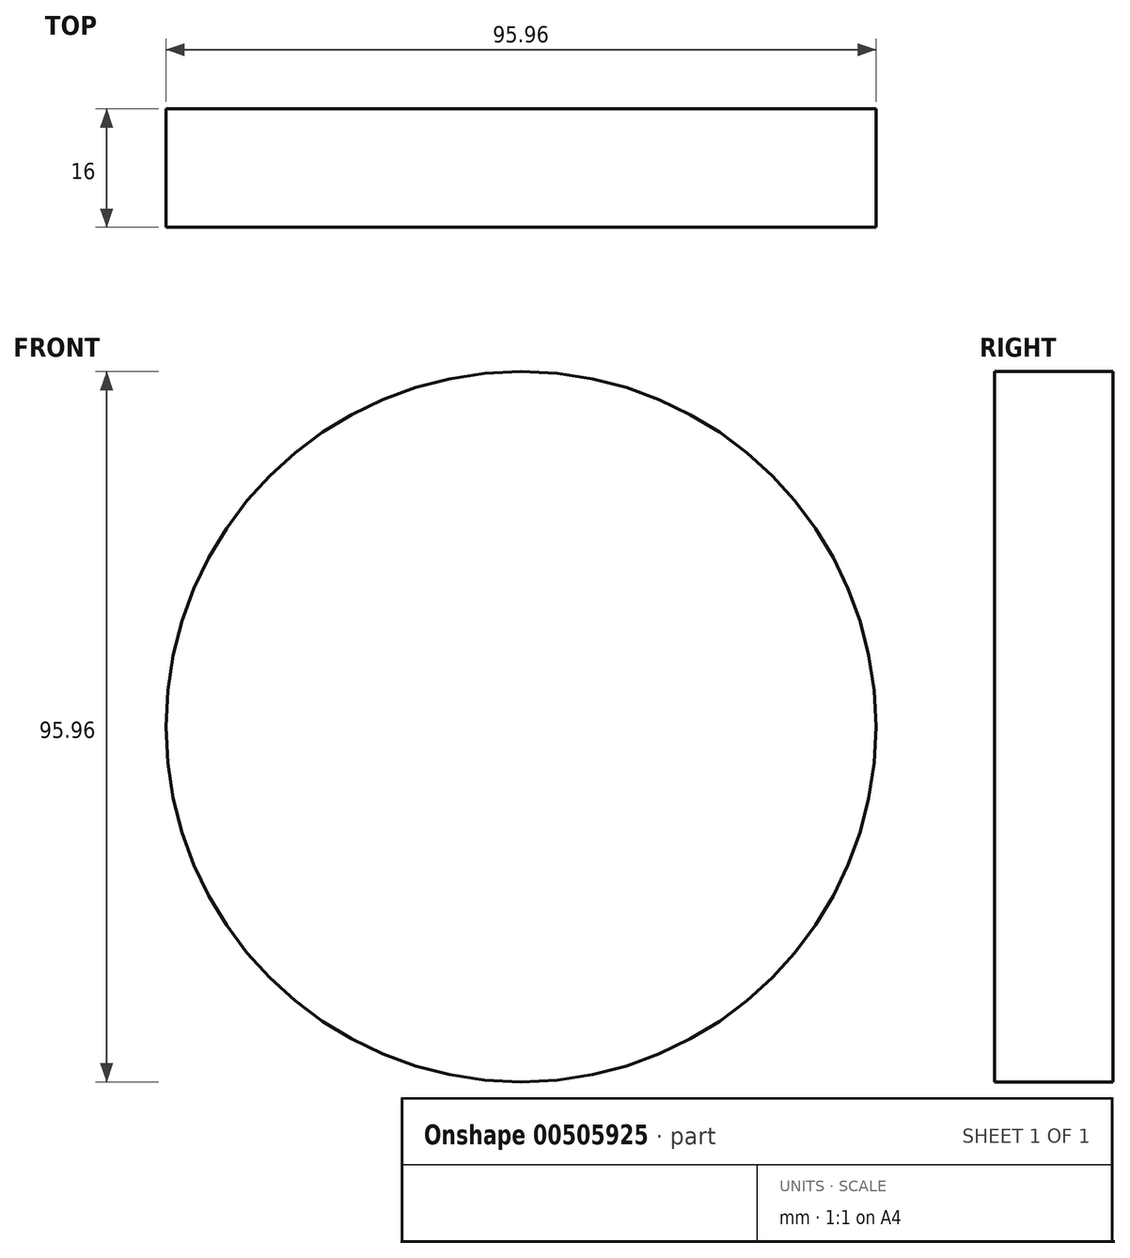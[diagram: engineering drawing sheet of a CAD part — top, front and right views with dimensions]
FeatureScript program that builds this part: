
annotation { "Feature Type Name" : "Feature", "Feature Type Description" : "" }
export const myFeature = defineFeature(function(context is Context, id is Id, definition is map)
    precondition{}
    {
        {
            var Q0;
            Q0=qCreatedBy(makeId("Front.planeOp"),FACE);
            var sketch = newSketch(context, id + "F0", { "sketchPlane" : qUnion([Q0])});
            skCircle(sketch, "E0", {"center": v(0, 0) * mm, "radius": 47.98 * mm});
            skSolve(sketch);
        }
        {
            var Q0;
            Q0 = qSketchRegion(id + "F0", true);
            extrude(context, id + "F1", {"entities" : qUnion([Q0]), "depth" : 16 * mm});
        }
    });
